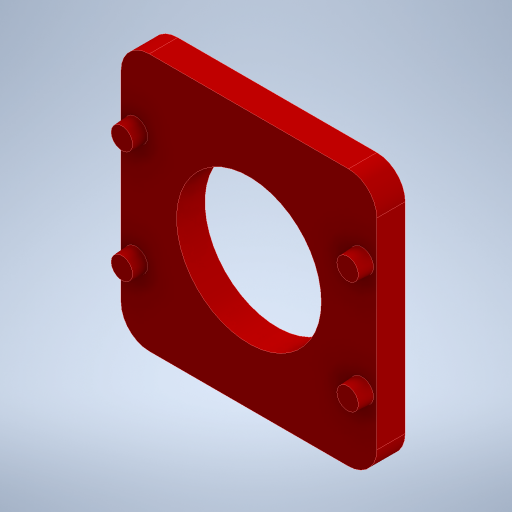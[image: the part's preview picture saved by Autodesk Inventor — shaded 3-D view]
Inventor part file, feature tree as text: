
AUTODESK INVENTOR PART (.ipt)
format: ipt  version: 2023.1 (Build 271208000, 208)  size: 260,608 bytes
history: native  units: mm
features: chamfer x4, extrude x2, sketch x2, reference x2, other x2
ambient origin geometry x8: Origin, YZ Plane, XZ Plane, XY Plane, X Axis, Y Axis, Z Axis, Center Point
bodies: Solid1 (feature_tree)
feature tree (12):
  extrude  "Extrusion1"  Depth=25.5mm
  extrude  "Extrusion2"  Depth=5.0mm TaperAngle=0.0deg
  chamfer  "Chamfer1"  Distance=2.5mm
  chamfer  "Chamfer2"  Distance=2.5mm
  chamfer  "Chamfer3"  Distance=2.5mm
  chamfer  "Chamfer4"  Distance=2.5mm
  sketch  "Sketch1"  dims[d0=5.5mm d1=25.5mm]
  reference  "Reference1"
  sketch  "Sketch2"  dims[d2=5.0mm d3=5.0mm d4=0.0mm d5=2.5mm d6=0.0mm d7=2.5mm d8=2.0mm d9=0.654498mm d10=2.5mm d11=2.0mm d12=0.654498mm d13=2.5mm d14=2.0mm d15=0.654498mm d16=2.5mm d17=2.0mm d18=0.654498mm]
  reference  "Reference2"
  other  "Cube 1x1 V5.iam"
  other  "Cube 1x1 Bottom V5:1"
